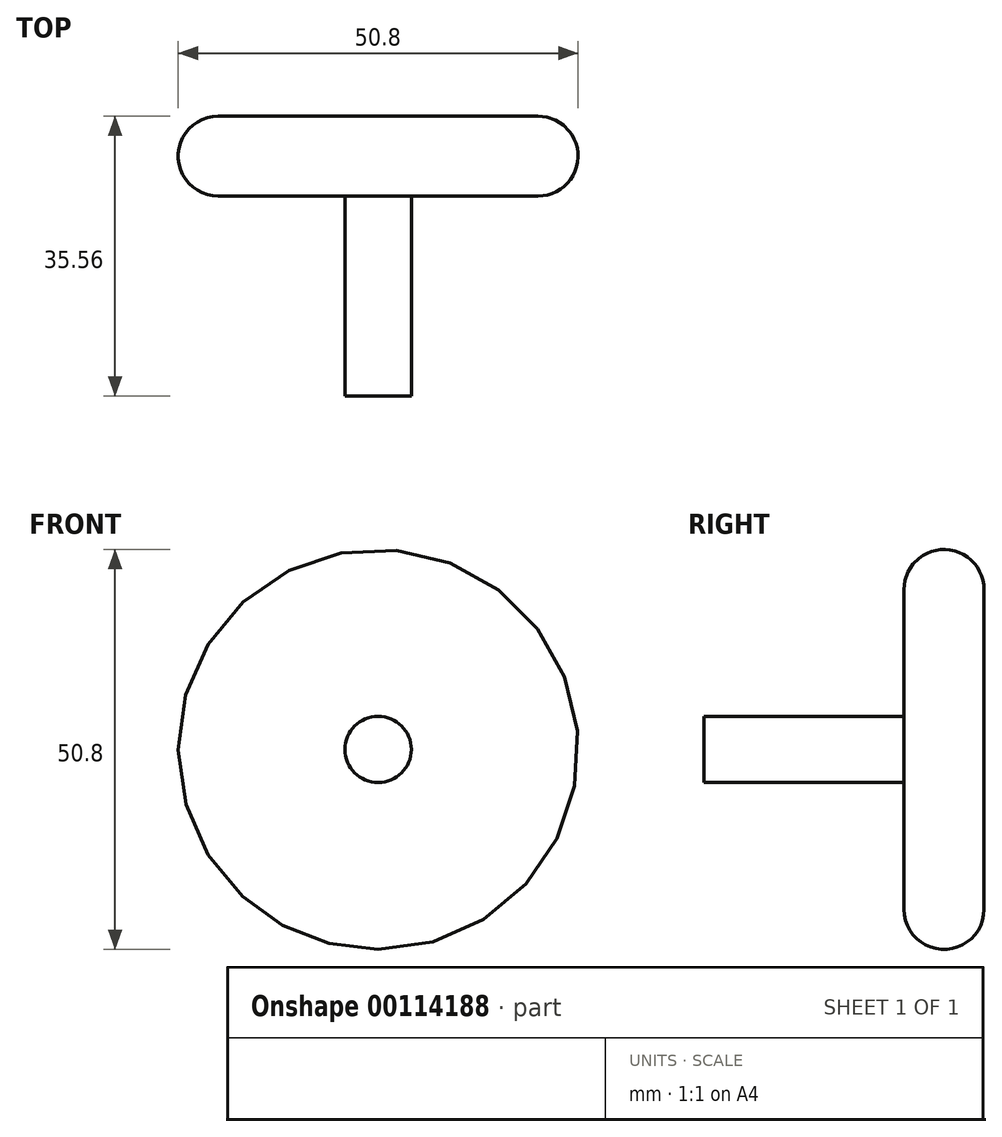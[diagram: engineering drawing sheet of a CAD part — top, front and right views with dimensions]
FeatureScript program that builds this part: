
annotation { "Feature Type Name" : "Feature", "Feature Type Description" : "" }
export const myFeature = defineFeature(function(context is Context, id is Id, definition is map)
    precondition{}
    {
        {
            var Q0;
            Q0=qCreatedBy(makeId("Front.planeOp"),FACE);
            var sketch = newSketch(context, id + "F0", { "sketchPlane" : qUnion([Q0])});
            skCircle(sketch, "E0", {"center": v(0, 0) * mm, "radius": 25.4 * mm});
            skSolve(sketch);
        }
        {
            var Q0;
            Q0=qSketchRegion(id+"F0",true);
            extrude(context, id + "F1", {"entities" : qUnion([Q0]), "depth" : 10.16 * mm});
        }
        {
            var Q0;
            Q0=makeQuery(id+"F1.opExtrude","CAP_EDGE",EDGE,{"disambiguationData":[OSD([sQuery(id+"F0.wireOp",EDGE,"E0")])],"isStart":false});
            fillet(context, id + "F2", {"entities" : qUnion([Q0]), "radius" : 5.08 * mm, "tangentPropagation" : true, "allowEdgeOverflow" : false});
        }
        {
            var Q0;
            Q0=makeQuery(id+"F1.opExtrude","CAP_EDGE",EDGE,{"disambiguationData":[OSD([sQuery(id+"F0.wireOp",EDGE,"E0")])],"isStart":true});
            fillet(context, id + "F3", {"entities" : qUnion([Q0]), "radius" : 5.08 * mm, "tangentPropagation" : true, "allowEdgeOverflow" : false});
        }
        {
            var Q0;
            Q0=makeQuery(id+"F1.opExtrude","CAP_FACE",FACE,{"disambiguationData":[OSD([sQuery(id+"F0.wireOp",EDGE,"E0")])],"isStart":false});
            var sketch = newSketch(context, id + "F4", { "sketchPlane" : qUnion([Q0])});
            skCircle(sketch, "E1", {"center": v(0, 0) * mm, "radius": 4.22 * mm});
            skSolve(sketch);
        }
        {
            var Q0;
            Q0=makeQuery(id+"F4.imprint","IMPRINT",FACE,{"disambiguationData":[TD([[makeQuery(id+"F4.imprint","IMPRINT",EDGE,{"derivedFrom":sQuery(id+"F4.wireOp",EDGE,"E1")}),1.0]])]});
            extrude(context, id + "F5", {"entities" : qUnion([Q0]), "operationType" : NewBodyOperationType.ADD, "depth" : 25.4 * mm});
        }
    });
